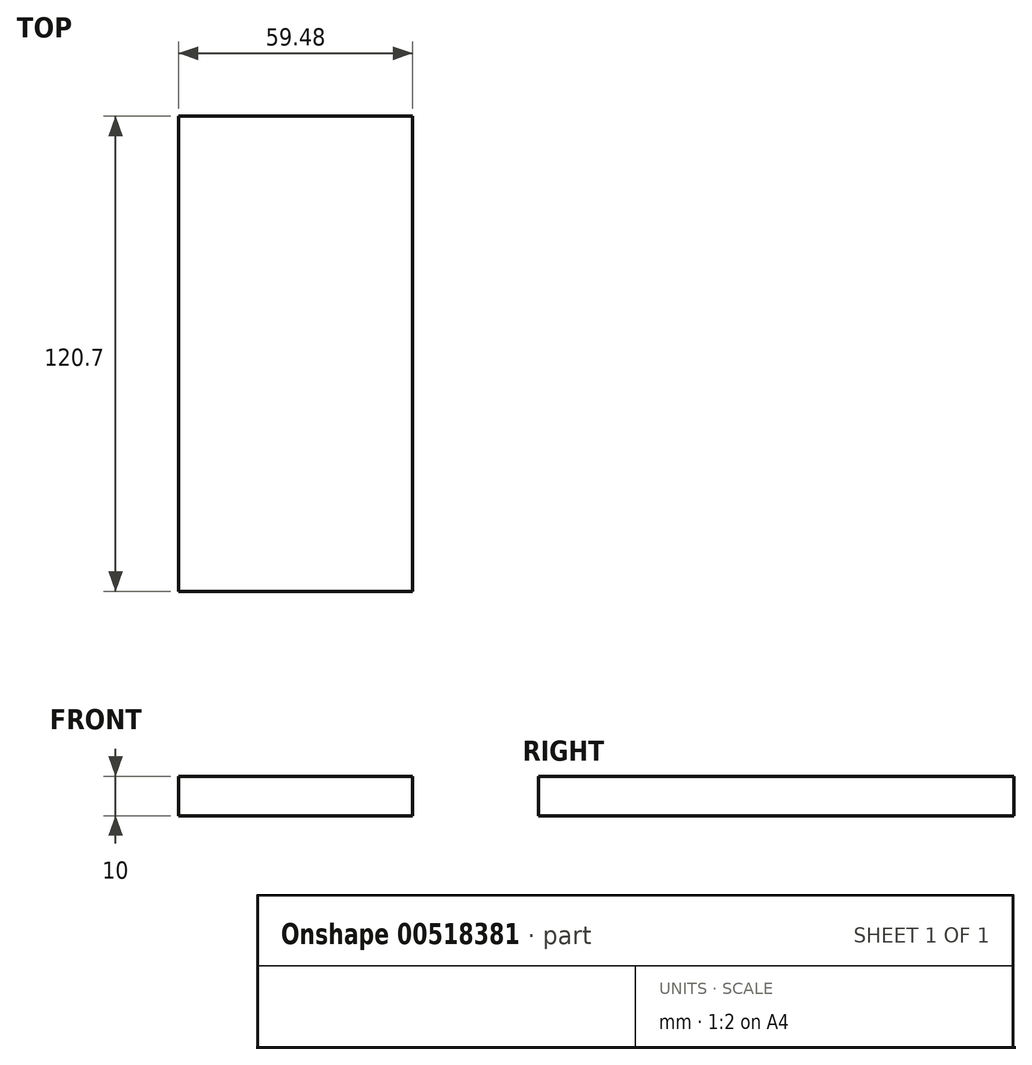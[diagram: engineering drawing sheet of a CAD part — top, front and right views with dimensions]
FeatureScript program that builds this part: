
annotation { "Feature Type Name" : "Feature", "Feature Type Description" : "" }
export const myFeature = defineFeature(function(context is Context, id is Id, definition is map)
    precondition{}
    {
        {
            var Q0;
            Q0=qCreatedBy(makeId("Top.planeOp"),FACE);
            var sketch = newSketch(context, id + "F0", { "sketchPlane" : qUnion([Q0])});
            skLineSegment(sketch, "E0.bottom", {"start": v(29.74, -60.35) * mm, "end": v(-29.74, -60.35) * mm});
            skLineSegment(sketch, "E0.top", {"start": v(29.74, 60.35) * mm, "end": v(-29.74, 60.35) * mm});
            skLineSegment(sketch, "E0.left", {"start": v(29.74, -60.35) * mm, "end": v(29.74, 60.35) * mm});
            skLineSegment(sketch, "E0.right", {"start": v(-29.74, -60.35) * mm, "end": v(-29.74, 60.35) * mm});
            skPoint(sketch, "E0.middle", {"position": v(0, 0) * mm});
            skSolve(sketch);
        }
        {
            var Q0;
            Q0 = qSketchRegion(id + "F0", true);
            extrude(context, id + "F1", {"entities" : qUnion([Q0]), "depth" : 10 * mm, "offsetDistance" : 25 * mm});
        }
    });
